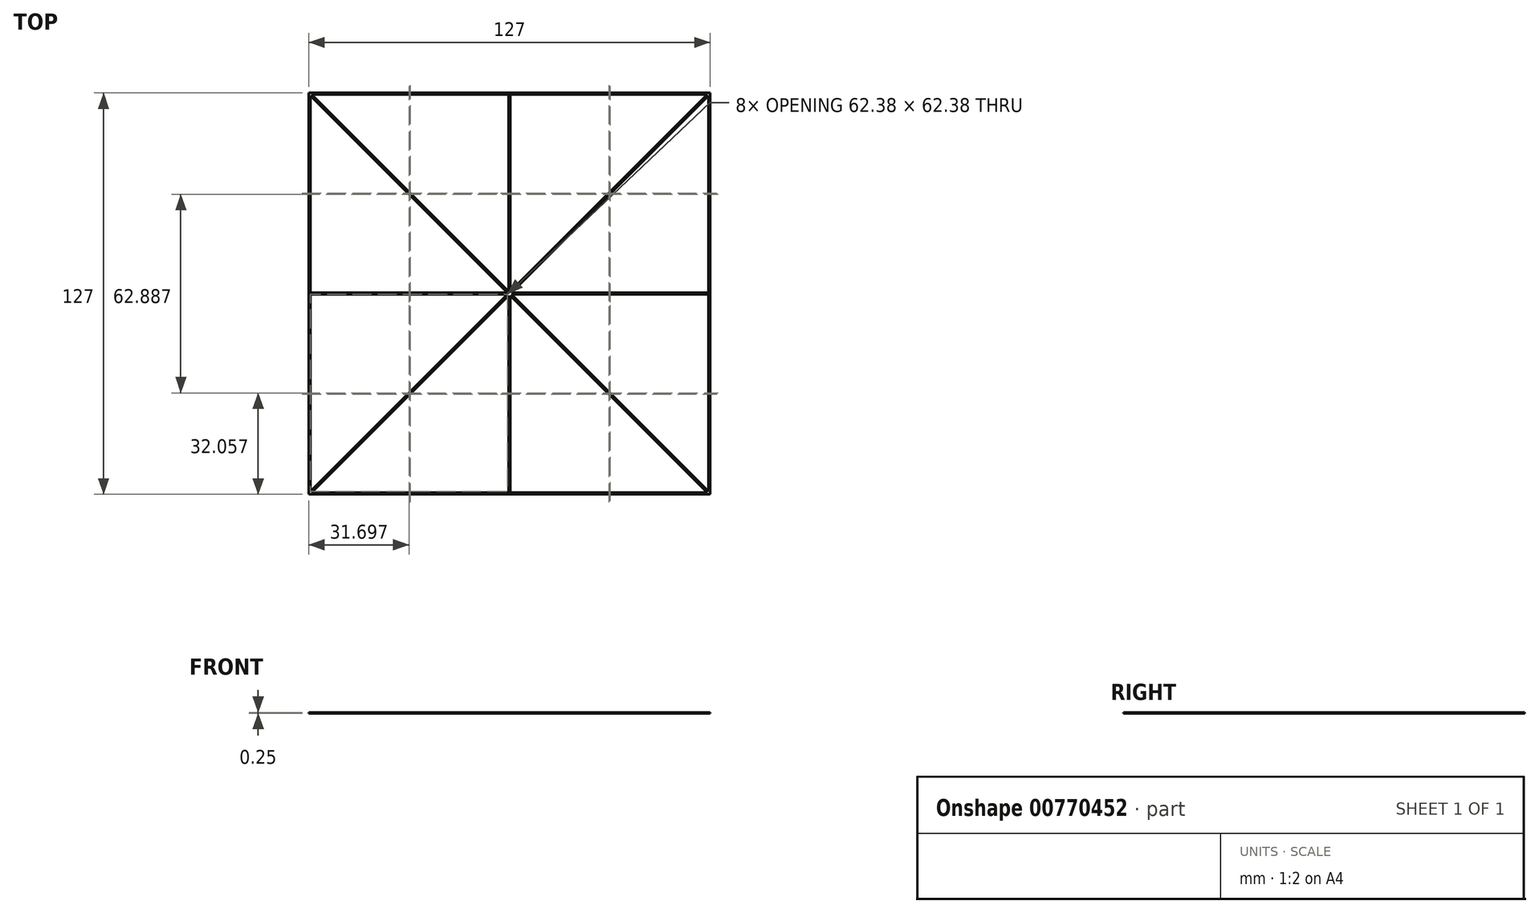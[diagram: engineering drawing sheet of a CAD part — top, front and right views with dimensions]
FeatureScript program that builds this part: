
annotation { "Feature Type Name" : "Feature", "Feature Type Description" : "" }
export const myFeature = defineFeature(function(context is Context, id is Id, definition is map)
    precondition{}
    {
        {
            var Q0;
            Q0=qCreatedBy(makeId("Top.planeOp"),FACE);
            var sketch = newSketch(context, id + "F0", { "sketchPlane" : qUnion([Q0])});
            skLineSegment(sketch, "E0.bottom", {"start": v(-63.5, -63.5) * mm, "end": v(63.5, -63.5) * mm, "construction": true});
            skLineSegment(sketch, "E0.top", {"start": v(-63.5, 63.5) * mm, "end": v(63.5, 63.5) * mm, "construction": true});
            skLineSegment(sketch, "E0.left", {"start": v(-63.5, -63.5) * mm, "end": v(-63.5, 63.5) * mm, "construction": true});
            skLineSegment(sketch, "E0.right", {"start": v(63.5, -63.5) * mm, "end": v(63.5, 63.5) * mm, "construction": true});
            skPoint(sketch, "E0.middle", {"position": v(0, 0) * mm});
            skLineSegment(sketch, "E1.bottom", {"start": v(-63, -63) * mm, "end": v(63, -63) * mm, "construction": true});
            skLineSegment(sketch, "E1.top", {"start": v(-63, 63) * mm, "end": v(63, 63) * mm, "construction": true});
            skLineSegment(sketch, "E1.left", {"start": v(-63, -63) * mm, "end": v(-63, 63) * mm, "construction": true});
            skLineSegment(sketch, "E1.right", {"start": v(63, -63) * mm, "end": v(63, 63) * mm, "construction": true});
            skLineSegment(sketch, "E2", {"start": v(0, 0) * mm, "end": v(0, 63) * mm, "construction": true});
            skLineSegment(sketch, "E3", {"start": v(-63, 63) * mm, "end": v(63, -63) * mm, "construction": true});
            skLineSegment(sketch, "E4", {"start": v(-63, -63) * mm, "end": v(63, 63) * mm, "construction": true});
            skLineSegment(sketch, "E5", {"start": v(0, 0) * mm, "end": v(-63, 0) * mm, "construction": true});
            skLineSegment(sketch, "E6", {"start": v(-0.25, 63) * mm, "end": v(-0.25, -63) * mm, "construction": true});
            skLineSegment(sketch, "E7", {"start": v(0.25, 63) * mm, "end": v(0.25, -63) * mm, "construction": true});
            skLineSegment(sketch, "E8", {"start": v(62.63, 63) * mm, "end": v(-63, -62.63) * mm, "construction": true});
            skLineSegment(sketch, "E9.0", {"start": v(63, 62.63) * mm, "end": v(-62.63, -63) * mm, "construction": true});
            skLineSegment(sketch, "E10.0", {"start": v(-63, 62.63) * mm, "end": v(62.63, -63) * mm, "construction": true});
            skLineSegment(sketch, "E11.0", {"start": v(-62.63, 63) * mm, "end": v(63, -62.63) * mm, "construction": true});
            skLineSegment(sketch, "E12.0", {"start": v(63, 0.25) * mm, "end": v(-63, 0.25) * mm, "construction": true});
            skLineSegment(sketch, "E13.0", {"start": v(63, -0.25) * mm, "end": v(-63, -0.25) * mm, "construction": true});
            skSolve(sketch);
        }
        {
            var Q0;
            Q0=qCreatedBy(makeId("Top.planeOp"),FACE);
            var sketch = newSketch(context, id + "F1", { "sketchPlane" : qUnion([Q0])});
            skPoint(sketch, "E14.middle", {"position": v(0, 0) * mm});
            skLineSegment(sketch, "E15.0", {"start": v(-63.5, 63.5) * mm, "end": v(63.5, 63.5) * mm});
            skLineSegment(sketch, "E16.1", {"start": v(63.5, -63.5) * mm, "end": v(63.5, 63.5) * mm});
            skLineSegment(sketch, "E17.1", {"start": v(-63.5, -63.5) * mm, "end": v(63.5, -63.5) * mm});
            skLineSegment(sketch, "E18.0", {"start": v(-63.5, -63.5) * mm, "end": v(-63.5, 63.5) * mm});
            skLineSegment(sketch, "E19.0", {"start": v(-62.63, 63) * mm, "end": v(-0.25, 63) * mm});
            skLineSegment(sketch, "E20.0", {"start": v(-0.25, 63) * mm, "end": v(-0.25, 0.61) * mm});
            skLineSegment(sketch, "E21.0", {"start": v(0.25, 63) * mm, "end": v(0.25, 0.61) * mm});
            skLineSegment(sketch, "E22.0", {"start": v(-63, -62.63) * mm, "end": v(-63, -0.25) * mm});
            skLineSegment(sketch, "E23.0", {"start": v(-62.63, 63) * mm, "end": v(-0.25, 0.61) * mm});
            skLineSegment(sketch, "E24.0", {"start": v(-63, 62.63) * mm, "end": v(-0.61, 0.25) * mm});
            skLineSegment(sketch, "E25.0", {"start": v(63, -62.63) * mm, "end": v(63, -0.25) * mm});
            skLineSegment(sketch, "E26.0", {"start": v(-62.63, -63) * mm, "end": v(-0.25, -63) * mm});
            skLineSegment(sketch, "E27.0", {"start": v(63, 62.63) * mm, "end": v(0.61, 0.25) * mm});
            skLineSegment(sketch, "E28.0", {"start": v(62.63, 63) * mm, "end": v(0.25, 0.61) * mm});
            skLineSegment(sketch, "E29.0", {"start": v(63, 0.25) * mm, "end": v(0.61, 0.25) * mm});
            skLineSegment(sketch, "E30.0", {"start": v(63, -0.25) * mm, "end": v(0.61, -0.25) * mm});
            skLineSegment(sketch, "E31.trimOffspring", {"start": v(0.25, 63) * mm, "end": v(62.63, 63) * mm});
            skLineSegment(sketch, "E32.trimOffspring", {"start": v(0.25, -63) * mm, "end": v(62.63, -63) * mm});
            skLineSegment(sketch, "E33.trimOffspring", {"start": v(63, 0.25) * mm, "end": v(63, 62.63) * mm});
            skLineSegment(sketch, "E34.trimOffspring", {"start": v(-63, 0.25) * mm, "end": v(-63, 62.63) * mm});
            skLineSegment(sketch, "E35.trimOffspring", {"start": v(-0.61, 0.25) * mm, "end": v(-63, 0.25) * mm});
            skLineSegment(sketch, "E36.trimOffspring", {"start": v(0.61, -0.25) * mm, "end": v(63, -62.63) * mm});
            skLineSegment(sketch, "E37.trimOffspring", {"start": v(0.25, -0.61) * mm, "end": v(0.25, -63) * mm});
            skLineSegment(sketch, "E38.trimOffspring", {"start": v(0.25, -0.61) * mm, "end": v(62.63, -63) * mm});
            skLineSegment(sketch, "E39.trimOffspring", {"start": v(-0.25, -0.61) * mm, "end": v(-62.63, -63) * mm});
            skLineSegment(sketch, "E40.trimOffspring", {"start": v(-0.61, -0.25) * mm, "end": v(-63, -62.63) * mm});
            skLineSegment(sketch, "E41.trimOffspring", {"start": v(-0.61, -0.25) * mm, "end": v(-63, -0.25) * mm});
            skLineSegment(sketch, "E42.trimOffspring", {"start": v(-0.25, -0.61) * mm, "end": v(-0.25, -63) * mm});
            skPoint(sketch, "E43.orphan", {"position": v(-63, 63) * mm});
            skPoint(sketch, "E44.orphan", {"position": v(63, 63) * mm});
            skPoint(sketch, "E45.orphan", {"position": v(63, -63) * mm});
            skPoint(sketch, "E46.orphan", {"position": v(-63, -63) * mm});
            skSolve(sketch);
        }
        {
            var Q0;
            Q0=qSketchRegion(id+"F1",true);
            extrude(context, id + "F2", {"entities" : qUnion([Q0]), "depth" : 0.25 * mm, "offsetDistance" : 25.4 * mm});
        }
    });
